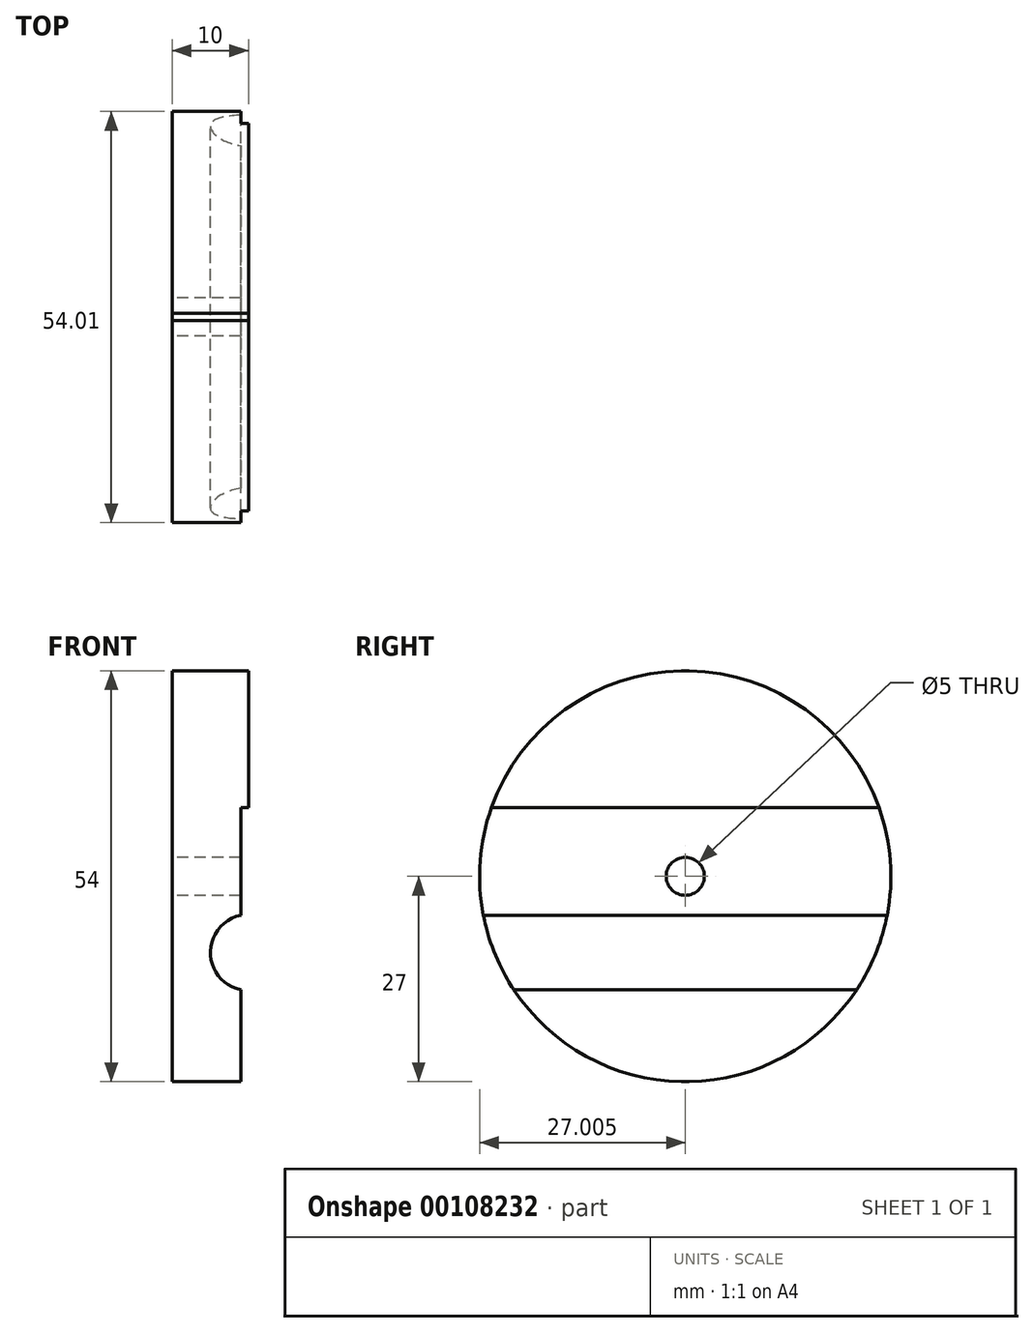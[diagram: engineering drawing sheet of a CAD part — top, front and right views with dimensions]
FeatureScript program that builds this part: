
annotation { "Feature Type Name" : "Feature", "Feature Type Description" : "" }
export const myFeature = defineFeature(function(context is Context, id is Id, definition is map)
    precondition{}
    {
        {
            var Q0;
            Q0=qCreatedBy(makeId("Front.planeOp"),FACE);
            var sketch = newSketch(context, id + "F0", { "sketchPlane" : qUnion([Q0])});
            skArc(sketch, "E0", {"start": v(1, 6.93) * mm, "mid": v(7, 0) * mm, "end": v(1, -6.93) * mm});
            skLineSegment(sketch, "E1", {"start": v(0, 19) * mm, "end": v(0, 37) * mm});
            skLineSegment(sketch, "E2", {"start": v(0, 37) * mm, "end": v(12, 37) * mm});
            skLineSegment(sketch, "E3", {"start": v(12, 37) * mm, "end": v(12, -17) * mm});
            skLineSegment(sketch, "E4", {"start": v(12, -17) * mm, "end": v(1, -17) * mm});
            skLineSegment(sketch, "E5", {"start": v(1, -17) * mm, "end": v(1, -6.93) * mm});
            skLineSegment(sketch, "E6", {"start": v(1, 6.93) * mm, "end": v(1, -6.93) * mm, "construction": true});
            skCircle(sketch, "E7", {"center": v(0, 0) * mm, "radius": 7 * mm, "construction": true});
            skLineSegment(sketch, "E8", {"start": v(0, 0) * mm, "end": v(0, 19) * mm, "construction": true});
            skLineSegment(sketch, "E9", {"start": v(0, 7) * mm, "end": v(0, 13) * mm, "construction": true});
            skLineSegment(sketch, "E10", {"start": v(0, 10) * mm, "end": v(12, 10) * mm, "construction": true});
            skPoint(sketch, "E10.endSnap0", {"position": v(12, 10) * mm});
            skLineSegment(sketch, "E11", {"start": v(0, 0) * mm, "end": v(0, -14) * mm, "construction": true});
            skPoint(sketch, "E12", {"position": v(0, -7) * mm});
            skPoint(sketch, "E12.positionSnap0", {"position": v(0, -7) * mm});
            skLineSegment(sketch, "E13", {"start": v(0, 19) * mm, "end": v(1, 19) * mm});
            skLineSegment(sketch, "E14", {"start": v(1, 19) * mm, "end": v(1, 6.93) * mm});
            skSolve(sketch);
        }
        {
            var Q0;
            Q0=makeQuery(id+"F0.imprint","IMPRINT",FACE,{"disambiguationData":[TD([[makeQuery(id+"F0.imprint","IMPRINT",EDGE,{"derivedFrom":sQuery(id+"F0.wireOp",EDGE,"E0")}),1.0]])]});
            var Q1;
            {var subQ0=sQuery(id+"F0.wireOp",EDGE,"E2");Q1=makeQuery(id+"F0.imprint","IMPRINT",FACE,{"disambiguationData":[TD([[makeQuery(id+"F0.imprint","IMPRINT",EDGE,{"derivedFrom":subQ0}),-1.0]])]});}
            extrude(context, id + "F1", {"entities" : qUnion([Q0, Q1]), "depth" : 55 * mm});
        }
        {
            var Q0;
            Q0=makeQuery(id+"F1.opExtrude","SWEPT_FACE",FACE,{"disambiguationData":[OSD([sQuery(id+"F0.wireOp",EDGE,"E3")])]});
            var sketch = newSketch(context, id + "F2", { "sketchPlane" : qUnion([Q0])});
            skCircle(sketch, "E15", {"center": v(-27, 10) * mm, "radius": 27 * mm});
            skPoint(sketch, "E15.first.point", {"position": v(-27.5, 37) * mm});
            skPoint(sketch, "E15.second.point", {"position": v(0, 10) * mm});
            skPoint(sketch, "E15.third.point", {"position": v(-27.5, -17) * mm});
            skSolve(sketch);
        }
        {
            var Q0;
            Q0=sQuery(id+"F2.wireOp",VERTEX,"E15.center");
            var Q1;
            Q1=makeQuery(id+"F1.opExtrude","SWEPT_BODY",BODY,{"disambiguationData":[OSD([sQuery(id+"F0.wireOp",EDGE,"E0"),sQuery(id+"F0.wireOp",EDGE,"E1"),sQuery(id+"F0.wireOp",EDGE,"E2"),sQuery(id+"F0.wireOp",EDGE,"E3"),sQuery(id+"F0.wireOp",EDGE,"E4"),sQuery(id+"F0.wireOp",EDGE,"E5")])]});
            hole(context, id + "F3", {"style" : HoleStyle.SIMPLE, "endStyle" : HoleEndStyle.THROUGH, "holeDiameter" : 5 * mm, "locations" : qUnion([Q0]), "scope" : qUnion([Q1]), "isTappedThrough" : true});
        }
        {
            var Q0;
            {var subQ0=sQuery(id+"F2.wireOp",EDGE,"E15");var subQ1=sQuery(id+"F0.wireOp",EDGE,"E3");var subQ3=makeQuery(id+"F2.imprint","INTERSECT",VERTEX,{"derivedFrom":[makeQuery(id+"F1.opExtrude","CAP_EDGE",EDGE,{"disambiguationData":[OSD([subQ1])],"isStart":true}),subQ0]});Q0=makeQuery(id+"F2.imprint","IMPRINT",FACE,{"disambiguationData":[TD([[makeQuery(id+"F2.imprint","IMPRINT",EDGE,{"disambiguationData":[TD([[subQ3,-1.0]])],"derivedFrom":subQ0}),1.0]])]});}
            extrude(context, id + "F4", {"entities" : qUnion([Q0]), "operationType" : NewBodyOperationType.INTERSECT, "endBound" : BoundingType.UP_TO_NEXT, "oppositeDirection" : true, "depth" : 25 * mm});
        }
        {
            var Q0;
            Q0=qCreatedBy(makeId("Front.planeOp"),FACE);
            var sketch = newSketch(context, id + "F5", { "sketchPlane" : qUnion([Q0])});
            skCircle(sketch, "E16", {"center": v(0, 0) * mm, "radius": 5 * mm, "construction": true});
            skArc(sketch, "E17", {"start": v(-1, 4.9) * mm, "mid": v(-5, 0) * mm, "end": v(-1, -4.9) * mm});
            skLineSegment(sketch, "E18", {"start": v(0, 19) * mm, "end": v(0, 37) * mm});
            skLineSegment(sketch, "E19", {"start": v(0, 37) * mm, "end": v(-10, 37) * mm});
            skLineSegment(sketch, "E20", {"start": v(-10, 37) * mm, "end": v(-10, -17) * mm});
            skLineSegment(sketch, "E21", {"start": v(-10, -17) * mm, "end": v(-1, -17) * mm});
            skLineSegment(sketch, "E22", {"start": v(-1, -17) * mm, "end": v(-1, -4.9) * mm});
            skLineSegment(sketch, "E23", {"start": v(-1, -4.9) * mm, "end": v(-1, 4.9) * mm, "construction": true});
            skLineSegment(sketch, "E24", {"start": v(0, 0) * mm, "end": v(0, 19) * mm, "construction": true});
            skLineSegment(sketch, "E25", {"start": v(0, 5) * mm, "end": v(0, 15) * mm, "construction": true});
            skLineSegment(sketch, "E26", {"start": v(0, 10) * mm, "end": v(-10, 10) * mm, "construction": true});
            skLineSegment(sketch, "E27", {"start": v(0, 0) * mm, "end": v(0, -5) * mm, "construction": true});
            skLineSegment(sketch, "E28", {"start": v(-1, 4.9) * mm, "end": v(-1, 19) * mm});
            skLineSegment(sketch, "E29", {"start": v(-1, 19) * mm, "end": v(0, 19) * mm});
            skSolve(sketch);
        }
        {
            var Q0;
            Q0=qSketchRegion(id+"F5",true);
            extrude(context, id + "F6", {"entities" : qUnion([Q0]), "depth" : 55 * mm});
        }
        {
            var Q0;
            Q0=makeQuery(id+"F6.opExtrude","SWEPT_FACE",FACE,{"disambiguationData":[OSD([sQuery(id+"F5.wireOp",EDGE,"E20")])]});
            var sketch = newSketch(context, id + "F7", { "sketchPlane" : qUnion([Q0])});
            skCircle(sketch, "E30", {"center": v(27, 10) * mm, "radius": 27 * mm});
            skPoint(sketch, "E30.first.point", {"position": v(0, 10) * mm});
            skPoint(sketch, "E30.second.point", {"position": v(27.5, 37) * mm});
            skPoint(sketch, "E30.third.point", {"position": v(27.5, -17) * mm});
            skSolve(sketch);
        }
        {
            var Q0;
            {var subQ0=sQuery(id+"F7.wireOp",EDGE,"E30");var subQ1=sQuery(id+"F5.wireOp",EDGE,"E20");var subQ5=makeQuery(id+"F7.imprint","INTERSECT",VERTEX,{"derivedFrom":[makeQuery(id+"F6.opExtrude","CAP_EDGE",EDGE,{"disambiguationData":[OSD([subQ1])],"isStart":true}),subQ0]});Q0=makeQuery(id+"F7.imprint","IMPRINT",FACE,{"disambiguationData":[TD([[makeQuery(id+"F7.imprint","IMPRINT",EDGE,{"disambiguationData":[TD([[subQ5,1.0]])],"derivedFrom":subQ0}),1.0]])]});}
            extrude(context, id + "F8", {"entities" : qUnion([Q0]), "operationType" : NewBodyOperationType.INTERSECT, "endBound" : BoundingType.UP_TO_NEXT, "oppositeDirection" : true, "depth" : 25 * mm});
        }
        {
            var Q0;
            Q0=sQuery(id+"F7.wireOp",VERTEX,"E30.center");
            var Q1;
            Q1=makeQuery(id+"F6.opExtrude","SWEPT_BODY",BODY,{"disambiguationData":[OSD([sQuery(id+"F5.wireOp",EDGE,"E17"),sQuery(id+"F5.wireOp",EDGE,"E18"),sQuery(id+"F5.wireOp",EDGE,"E19"),sQuery(id+"F5.wireOp",EDGE,"E20"),sQuery(id+"F5.wireOp",EDGE,"E21"),sQuery(id+"F5.wireOp",EDGE,"E22")])]});
            hole(context, id + "F9", {"style" : HoleStyle.SIMPLE, "endStyle" : HoleEndStyle.THROUGH, "holeDiameter" : 5 * mm, "locations" : qUnion([Q0]), "scope" : qUnion([Q1]), "isTappedThrough" : true});
        }
    });
